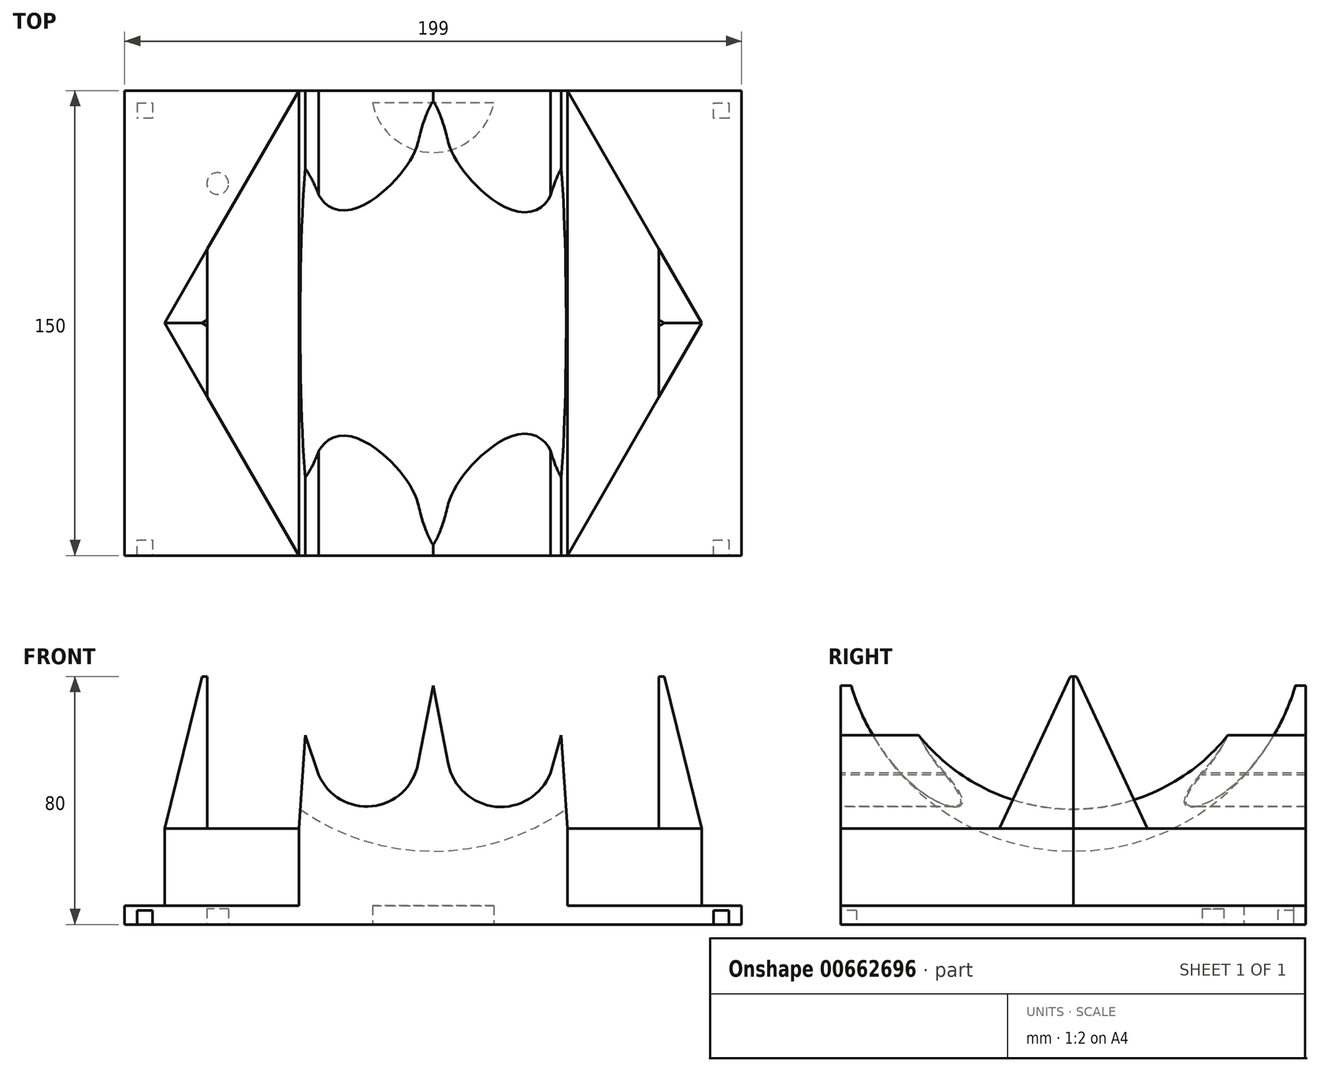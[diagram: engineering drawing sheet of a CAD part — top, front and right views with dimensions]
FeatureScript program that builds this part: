
annotation { "Feature Type Name" : "Feature", "Feature Type Description" : "" }
export const myFeature = defineFeature(function(context is Context, id is Id, definition is map)
    precondition{}
    {
        {
            var Q0;
            Q0=qCreatedBy(makeId("Top.planeOp"),FACE);
            var sketch = newSketch(context, id + "F0", { "sketchPlane" : qUnion([Q0])});
            skLineSegment(sketch, "E0.bottom", {"start": v(-99.5, 75) * mm, "end": v(99.5, 75) * mm});
            skLineSegment(sketch, "E0.left", {"start": v(-99.5, 75) * mm, "end": v(-99.5, -75) * mm});
            skLineSegment(sketch, "E0.right", {"start": v(99.5, 75) * mm, "end": v(99.5, -75) * mm});
            skPoint(sketch, "E0.middle", {"position": v(0, 0) * mm});
            skLineSegment(sketch, "E1.1", {"start": v(-95.5, 71) * mm, "end": v(-95.5, -70) * mm});
            skLineSegment(sketch, "E1.2", {"start": v(-95.5, 71) * mm, "end": v(95.4, 71) * mm});
            skLineSegment(sketch, "E1.3", {"start": v(95.4, 71) * mm, "end": v(95.4, -70) * mm});
            skLineSegment(sketch, "E2", {"start": v(0, -75) * mm, "end": v(0, -73) * mm});
            skPoint(sketch, "E2.endSnap0", {"position": v(0, -75) * mm});
            skPoint(sketch, "E3.end.orphan", {"position": v(95.5, 0) * mm});
            skLineSegment(sketch, "E4", {"start": v(-99.5, -75) * mm, "end": v(-95.5, -75) * mm});
            skLineSegment(sketch, "E5", {"start": v(-95.5, -75) * mm, "end": v(-95.5, -70) * mm});
            skLineSegment(sketch, "E6", {"start": v(95.4, -70) * mm, "end": v(95.4, -75) * mm});
            skLineSegment(sketch, "E7", {"start": v(95.4, -75) * mm, "end": v(99.5, -75) * mm});
            skPoint(sketch, "E8.end.orphan", {"position": v(-95.5, -70) * mm});
            skLineSegment(sketch, "E9", {"start": v(-90.5, 71) * mm, "end": v(-90.5, 66) * mm});
            skLineSegment(sketch, "E10", {"start": v(-90.5, 66) * mm, "end": v(-95.5, 66) * mm});
            skLineSegment(sketch, "E11", {"start": v(95.4, 66) * mm, "end": v(90.4, 66) * mm});
            skLineSegment(sketch, "E12", {"start": v(90.4, 66) * mm, "end": v(90.4, 71) * mm});
            skLineSegment(sketch, "E13", {"start": v(-95.5, 71) * mm, "end": v(-90.5, 71) * mm});
            skLineSegment(sketch, "E14", {"start": v(-95.5, 71) * mm, "end": v(-95.5, 66) * mm});
            skLineSegment(sketch, "E15", {"start": v(90.4, 71) * mm, "end": v(95.4, 71) * mm});
            skLineSegment(sketch, "E16", {"start": v(95.4, 66) * mm, "end": v(95.4, 71) * mm});
            skLineSegment(sketch, "E17", {"start": v(95.4, -75) * mm, "end": v(90.4, -75) * mm});
            skLineSegment(sketch, "E18", {"start": v(90.4, -75) * mm, "end": v(90.4, -70) * mm});
            skLineSegment(sketch, "E19", {"start": v(90.4, -70) * mm, "end": v(95.4, -70) * mm});
            skLineSegment(sketch, "E20", {"start": v(-95.5, -70) * mm, "end": v(-90.5, -70) * mm});
            skLineSegment(sketch, "E21", {"start": v(-95.5, -75) * mm, "end": v(-90.5, -75) * mm});
            skLineSegment(sketch, "E22", {"start": v(-90.5, -70) * mm, "end": v(-90.5, -75) * mm});
            skLineSegment(sketch, "E23", {"start": v(0, 73) * mm, "end": v(0, 71) * mm});
            skPoint(sketch, "E24.MirrorCS.end.orphan", {"position": v(-8.62, 71) * mm});
            skPoint(sketch, "E24.MirrorCS.start.orphan", {"position": v(8.62, 71) * mm});
            skSolve(sketch);
        }
        {
            var Q0;
            Q0=qCreatedBy(makeId("Top.planeOp"),FACE);
            var sketch = newSketch(context, id + "F1", { "sketchPlane" : qUnion([Q0])});
            skLineSegment(sketch, "E25.bottom", {"start": v(-99.5, 75) * mm, "end": v(-20, 75) * mm});
            skLineSegment(sketch, "E25.top", {"start": v(-99.5, -75) * mm, "end": v(99.5, -75) * mm});
            skLineSegment(sketch, "E25.left", {"start": v(-99.5, 75) * mm, "end": v(-99.5, -75) * mm});
            skLineSegment(sketch, "E25.right", {"start": v(99.5, 75) * mm, "end": v(99.5, -75) * mm});
            skPoint(sketch, "E25.middle", {"position": v(0, 0) * mm});
            skCircle(sketch, "E26", {"center": v(-69.5, 45) * mm, "radius": 3.5 * mm});
            skLineSegment(sketch, "E27.trimOffspring", {"start": v(20, 75) * mm, "end": v(99.5, 75) * mm});
            skArc(sketch, "E28", {"start": v(-20, 75) * mm, "mid": v(0, 55) * mm, "end": v(20, 75) * mm});
            skLineSegment(sketch, "E29", {"start": v(-20, 75) * mm, "end": v(20, 75) * mm});
            skLineSegment(sketch, "E30", {"start": v(19.6, 71) * mm, "end": v(-19.6, 71) * mm});
            skSolve(sketch);
        }
        {
            var Q0;
            Q0=qSketchRegion(id+"F1",true);
            extrude(context, id + "F2", {"entities" : qUnion([Q0]), "depth" : 6 * mm, "offsetDistance" : 25 * mm});
        }
        {
            var Q0;
            Q0=makeQuery(id+"F0.imprint","IMPRINT",FACE,{"disambiguationData":[TD([[makeQuery(id+"F0.imprint","IMPRINT",EDGE,{"derivedFrom":sQuery(id+"F0.wireOp",EDGE,"E9")}),-1.0]])]});
            var Q1;
            Q1=makeQuery(id+"F0.imprint","IMPRINT",FACE,{"disambiguationData":[TD([[makeQuery(id+"F0.imprint","IMPRINT",EDGE,{"derivedFrom":sQuery(id+"F0.wireOp",EDGE,"E11")}),-1.0]])]});
            var Q2;
            Q2=makeQuery(id+"F0.imprint","IMPRINT",FACE,{"disambiguationData":[TD([[makeQuery(id+"F0.imprint","IMPRINT",EDGE,{"derivedFrom":sQuery(id+"F0.wireOp",EDGE,"E5")}),-1.0]])]});
            var Q3;
            Q3=makeQuery(id+"F0.imprint","IMPRINT",FACE,{"disambiguationData":[TD([[makeQuery(id+"F0.imprint","IMPRINT",EDGE,{"derivedFrom":sQuery(id+"F0.wireOp",EDGE,"E6")}),-1.0]])]});
            extrude(context, id + "F3", {"entities" : qUnion([Q0, Q1, Q2, Q3]), "operationType" : NewBodyOperationType.REMOVE, "depth" : 4.5 * mm, "offsetDistance" : 25 * mm});
        }
        {
            var Q0;
            Q0=makeQuery(id+"F0.imprint","IMPRINT",FACE,{"disambiguationData":[TD([[makeQuery(id+"F0.imprint","IMPRINT",EDGE,{"derivedFrom":sQuery(id+"F0.wireOp",EDGE,"E5")}),-1.0]])]});
            extrude(context, id + "F4", {"entities" : qUnion([Q0]), "operationType" : NewBodyOperationType.REMOVE, "depth" : 4.5 * mm, "offsetDistance" : 25 * mm});
        }
        {
            var Q0;
            Q0=makeQuery(id+"F2.opExtrude","CAP_FACE",FACE,{"disambiguationData":[OSD([sQuery(id+"F1.wireOp",EDGE,"E25.bottom"),sQuery(id+"F1.wireOp",EDGE,"E25.top"),sQuery(id+"F1.wireOp",EDGE,"E25.left"),sQuery(id+"F1.wireOp",EDGE,"E25.right"),sQuery(id+"F1.wireOp",EDGE,"E26"),sQuery(id+"F1.wireOp",EDGE,"E27.trimOffspring"),sQuery(id+"F1.wireOp",EDGE,"E28")])],"isStart":false});
            var sketch = newSketch(context, id + "F5", { "sketchPlane" : qUnion([Q0])});
            skCircle(sketch, "E31.cCircle", {"center": v(0, 0) * mm, "radius": 75 * mm, "construction": true});
            skLineSegment(sketch, "E31.0", {"start": v(-43.3, 75) * mm, "end": v(43.3, 75) * mm});
            skLineSegment(sketch, "E31.1", {"start": v(43.3, 75) * mm, "end": v(86.6, 0) * mm});
            skLineSegment(sketch, "E31.2", {"start": v(86.6, 0) * mm, "end": v(43.3, -75) * mm});
            skLineSegment(sketch, "E31.3", {"start": v(43.3, -75) * mm, "end": v(-43.3, -75) * mm});
            skLineSegment(sketch, "E31.4", {"start": v(-43.3, -75) * mm, "end": v(-86.6, 0) * mm});
            skLineSegment(sketch, "E31.5", {"start": v(-86.6, 0) * mm, "end": v(-43.3, 75) * mm});
            skPoint(sketch, "E31.0.midPoint", {"position": v(0, 75) * mm});
            skCircle(sketch, "E32", {"center": v(-69.5, 45) * mm, "radius": 3.84 * mm});
            skLineSegment(sketch, "E33", {"start": v(-69.5, 45) * mm, "end": v(-69.5, 75) * mm});
            skLineSegment(sketch, "E34", {"start": v(-69.5, 75) * mm, "end": v(-69.5, 41) * mm});
            skLineSegment(sketch, "E35", {"start": v(-69.5, 41) * mm, "end": v(-99.5, 41) * mm});
            skLineSegment(sketch, "E36", {"start": v(-99.5, 41) * mm, "end": v(-65.5, 41.18) * mm});
            skSolve(sketch);
        }
        {
            var Q0;
            Q0=makeQuery(id+"F5.imprint","IMPRINT",FACE,{"disambiguationData":[TD([[makeQuery(id+"F5.imprint","IMPRINT",EDGE,{"derivedFrom":makeQuery(id+"F2.opExtrude","CAP_EDGE",EDGE,{"disambiguationData":[OSD([sQuery(id+"F1.wireOp",EDGE,"E26")])],"isStart":false})}),1.0]])]});
            extrude(context, id + "F6", {"entities" : qUnion([Q0]), "operationType" : NewBodyOperationType.ADD, "oppositeDirection" : true, "depth" : 1 * mm, "offsetDistance" : 25 * mm});
        }
        {
            var Q0;
            {var subQ0=sQuery(id+"F5.wireOp",EDGE,"E31.1");Q0=makeQuery(id+"F5.imprint","IMPRINT",FACE,{"disambiguationData":[TD([[makeQuery(id+"F5.imprint","IMPRINT",EDGE,{"derivedFrom":subQ0}),-1.0]])]});}
            var Q1;
            {var subQ1=makeQuery(id+"F2.opExtrude","CAP_EDGE",EDGE,{"disambiguationData":[OSD([sQuery(id+"F1.wireOp",EDGE,"E28")])],"isStart":false});Q1=makeQuery(id+"F5.imprint","IMPRINT",FACE,{"disambiguationData":[TD([[makeQuery(id+"F5.imprint","IMPRINT",EDGE,{"derivedFrom":subQ1}),1.0]])]});}
            extrude(context, id + "F7", {"entities" : qUnion([Q0, Q1]), "operationType" : NewBodyOperationType.ADD, "depth" : 25 * mm, "offsetDistance" : 25 * mm});
        }
        {
            var Q0;
            Q0=makeQuery(id+"F7.boolean.opBoolean","MERGE",FACE,{"derivedFrom":[makeQuery(id+"F2.opExtrude","SWEPT_FACE",FACE,{"disambiguationData":[OSD([sQuery(id+"F1.wireOp",EDGE,"E25.top")])]}),makeQuery(id+"F7.opExtrude","SWEPT_FACE",FACE,{"disambiguationData":[OSD([sQuery(id+"F5.wireOp",EDGE,"E31.3")])]})]});
            var sketch = newSketch(context, id + "F8", { "sketchPlane" : qUnion([Q0])});
            skLineSegment(sketch, "E37", {"start": v(-43.3, 31) * mm, "end": v(43.3, 31) * mm});
            skLineSegment(sketch, "E38", {"start": v(-41.3, 61) * mm, "end": v(-43.3, 31) * mm});
            skLineSegment(sketch, "E39", {"start": v(-36.89, 48.16) * mm, "end": v(-41.3, 61) * mm});
            skLineSegment(sketch, "E40", {"start": v(4.9, 51.85) * mm, "end": v(-0.01, 77) * mm});
            skLineSegment(sketch, "E41", {"start": v(-4.94, 51.67) * mm, "end": v(-0.01, 77) * mm});
            skLineSegment(sketch, "E42", {"start": v(41.3, 61) * mm, "end": v(37.86, 48.79) * mm});
            skLineSegment(sketch, "E43", {"start": v(43.3, 31) * mm, "end": v(41.3, 61) * mm});
            skArc(sketch, "E44", {"start": v(-36.89, 48.16) * mm, "mid": v(-19.62, 38.15) * mm, "end": v(-4.94, 51.67) * mm});
            skArc(sketch, "E45", {"start": v(4.9, 51.85) * mm, "mid": v(20.24, 37.98) * mm, "end": v(37.86, 48.79) * mm});
            skSolve(sketch);
        }
        {
            var Q0;
            Q0=makeQuery(id+"F8.imprint","IMPRINT",FACE,{"disambiguationData":[TD([[makeQuery(id+"F8.imprint","IMPRINT",EDGE,{"derivedFrom":sQuery(id+"F8.wireOp",EDGE,"E37")}),1.0]])]});
            extrude(context, id + "F9", {"entities" : qUnion([Q0]), "operationType" : NewBodyOperationType.ADD, "oppositeDirection" : true, "depth" : 150 * mm, "offsetDistance" : 25 * mm});
        }
        {
            var Q0;
            Q0=qCreatedBy(makeId("Front.planeOp"),FACE);
            var sketch = newSketch(context, id + "F10", { "sketchPlane" : qUnion([Q0])});
            skArc(sketch, "E46", {"start": v(-74.77, 98.4) * mm, "mid": v(0, 23.62) * mm, "end": v(74.77, 98.4) * mm});
            skLineSegment(sketch, "E47", {"start": v(-91.46, 98.4) * mm, "end": v(102.43, 98.4) * mm});
            skSolve(sketch);
        }
        {
            var Q0;
            Q0 = qSketchRegion(id + "F10", true);
            var Q1;
            Q1=sQuery(id+"F10.wireOp",EDGE,"E47");
            revolve(context, id + "F11", {"operationType" : NewBodyOperationType.REMOVE, "entities" : qUnion([Q0]), "axis" : qUnion([Q1]), "revolveType" : RevolveType.FULL, "oppositeDirection" : true});
        }
        {
            var Q0;
            {var subQ0=sQuery(id+"F5.wireOp",EDGE,"E31.1");var subQ1=sQuery(id+"F5.wireOp",EDGE,"E31.0");var subQ3=sQuery(id+"F5.wireOp",EDGE,"E31.2");var subQ4=sQuery(id+"F5.wireOp",EDGE,"E31.3");Q0=makeQuery(id+"F9.boolean.opBoolean","SPLIT",FACE,{"disambiguationData":[TD([makeQuery(id+"F7.opExtrude","SWEPT_FACE",FACE,{"disambiguationData":[OSD([subQ0])]})])],"derivedFrom":makeQuery(id+"F7.opExtrude","CAP_FACE",FACE,{"disambiguationData":[OSD([subQ1,subQ0,subQ3,subQ4,sQuery(id+"F5.wireOp",EDGE,"E31.4"),sQuery(id+"F5.wireOp",EDGE,"E31.5")])],"isStart":false})});}
            var sketch = newSketch(context, id + "F12", { "sketchPlane" : qUnion([Q0])});
            skLineSegment(sketch, "E48", {"start": v(86.6, 0) * mm, "end": v(72.84, 23.84) * mm});
            skLineSegment(sketch, "E49", {"start": v(72.84, 23.84) * mm, "end": v(72.84, -23.84) * mm});
            skLineSegment(sketch, "E50", {"start": v(72.84, -23.84) * mm, "end": v(86.6, 0) * mm});
            skLineSegment(sketch, "E51.MirrorCS", {"start": v(-72.84, 23.84) * mm, "end": v(-72.84, -23.84) * mm});
            skLineSegment(sketch, "E52.MirrorCS", {"start": v(-86.6, 0) * mm, "end": v(-72.84, 23.84) * mm});
            skLineSegment(sketch, "E53.MirrorCS", {"start": v(-72.84, -23.84) * mm, "end": v(-86.6, 0) * mm});
            skSolve(sketch);
        }
        {
            var Q0;
            Q0=qCreatedBy(makeId("Top.planeOp"),FACE);
            cPlane(context, id + "F13", {"entities" : qUnion([Q0]), "cplaneType" : CPlaneType.OFFSET, "offset" : 80 * mm, "width" : 150 * mm, "height" : 150 * mm});
        }
        {
            var Q0;
            Q0=qCreatedBy(id+"F13.planeOp",FACE);
            var sketch = newSketch(context, id + "F14", { "sketchPlane" : qUnion([Q0])});
            skLineSegment(sketch, "E54", {"start": v(-74.52, 0) * mm, "end": v(-72.84, 1.05) * mm});
            skLineSegment(sketch, "E55", {"start": v(-72.84, 1.05) * mm, "end": v(-72.84, -0.99) * mm});
            skLineSegment(sketch, "E56", {"start": v(-72.84, -0.99) * mm, "end": v(-74.52, 0) * mm});
            skLineSegment(sketch, "E57.MirrorCS", {"start": v(74.52, 0) * mm, "end": v(72.84, 1.05) * mm});
            skLineSegment(sketch, "E58.MirrorCS", {"start": v(72.84, 1.05) * mm, "end": v(72.84, -0.99) * mm});
            skLineSegment(sketch, "E59.MirrorCS", {"start": v(72.84, -0.99) * mm, "end": v(74.52, 0) * mm});
            skSolve(sketch);
        }
        {
            var Q1;
            Q1=makeQuery(id+"F12.imprint","IMPRINT",FACE,{"disambiguationData":[TD([[makeQuery(id+"F12.imprint","IMPRINT",EDGE,{"derivedFrom":sQuery(id+"F12.wireOp",EDGE,"E51.MirrorCS")}),-1.0]])]});
            var Q2;
            Q2=makeQuery(id+"F14.imprint","IMPRINT",FACE,{"disambiguationData":[TD([[makeQuery(id+"F14.imprint","IMPRINT",EDGE,{"derivedFrom":sQuery(id+"F14.wireOp",EDGE,"E54")}),-1.0]])]});
            loft(context, id + "F15", {"operationType" : NewBodyOperationType.ADD, "sheetProfilesArray" : [{ "sheetProfileEntities" : qUnion([Q1]) }, { "sheetProfileEntities" : qUnion([Q2]) }]});
        }
        {
            var Q1;
            Q1=makeQuery(id+"F12.imprint","IMPRINT",FACE,{"disambiguationData":[TD([[makeQuery(id+"F12.imprint","IMPRINT",EDGE,{"derivedFrom":sQuery(id+"F12.wireOp",EDGE,"E48")}),-1.0]])]});
            var Q2;
            Q2=makeQuery(id+"F14.imprint","IMPRINT",FACE,{"disambiguationData":[TD([[makeQuery(id+"F14.imprint","IMPRINT",EDGE,{"derivedFrom":sQuery(id+"F14.wireOp",EDGE,"E57.MirrorCS")}),1.0]])]});
            loft(context, id + "F16", {"operationType" : NewBodyOperationType.ADD, "sheetProfilesArray" : [{ "sheetProfileEntities" : qUnion([Q1]) }, { "sheetProfileEntities" : qUnion([Q2]) }]});
        }
    });
